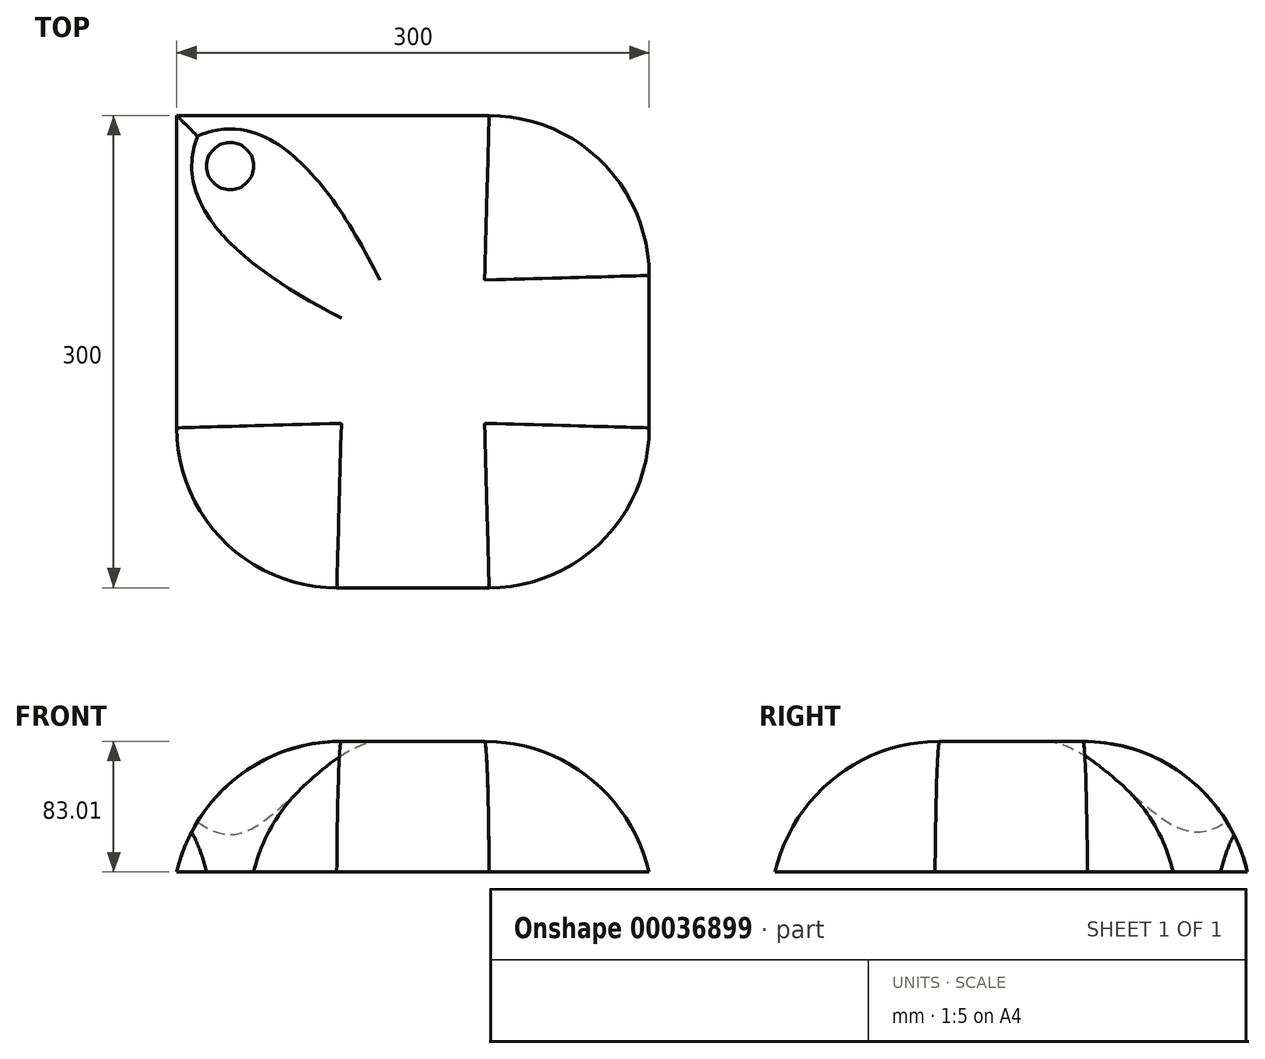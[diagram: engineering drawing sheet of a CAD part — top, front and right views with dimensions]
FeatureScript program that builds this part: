
annotation { "Feature Type Name" : "Feature", "Feature Type Description" : "" }
export const myFeature = defineFeature(function(context is Context, id is Id, definition is map)
    precondition{}
    {
        {
            var Q0;
            Q0=qCreatedBy(makeId("Top.planeOp"),FACE);
            var sketch = newSketch(context, id + "F0", { "sketchPlane" : qUnion([Q0])});
            skLineSegment(sketch, "E0.bottom", {"start": v(-153.37, 144.8) * mm, "end": v(146.63, 144.8) * mm});
            skLineSegment(sketch, "E0.top", {"start": v(-153.37, -155.2) * mm, "end": v(146.63, -155.2) * mm});
            skLineSegment(sketch, "E0.left", {"start": v(-153.37, 144.8) * mm, "end": v(-153.37, -155.2) * mm});
            skLineSegment(sketch, "E0.right", {"start": v(146.63, 144.8) * mm, "end": v(146.63, -155.2) * mm});
            skCircle(sketch, "E1", {"center": v(-119.5, 112.69) * mm, "radius": 15 * mm});
            skSolve(sketch);
        }
        {
            var Q0;
            Q0 = qSketchRegion(id + "F0", true);
            var Q1;
            Q1=makeQuery(id+"F0.imprint","IMPRINT",FACE,{"disambiguationData":[TD([[makeQuery(id+"F0.imprint","IMPRINT",EDGE,{"derivedFrom":sQuery(id+"F0.wireOp",EDGE,"E0.bottom")}),-1.0]])]});
            extrude(context, id + "F1", {"entities" : qUnion([Q0, Q1]), "depth" : 83.01 * mm});
        }
        {
            var Q0;
            Q0=makeQuery(id+"F1.opExtrude","SWEPT_EDGE",EDGE,{"disambiguationData":[OSD([sQuery(id+"F0.wireOp",EDGE,"E0.bottom"),sQuery(id+"F0.wireOp",EDGE,"E0.right")])]});
            var Q1;
            Q1=makeQuery(id+"F1.opExtrude","SWEPT_EDGE",EDGE,{"disambiguationData":[OSD([sQuery(id+"F0.wireOp",EDGE,"E0.top"),sQuery(id+"F0.wireOp",EDGE,"E0.left")])]});
            var Q2;
            Q2=makeQuery(id+"F1.opExtrude","SWEPT_EDGE",EDGE,{"disambiguationData":[OSD([sQuery(id+"F0.wireOp",EDGE,"E0.top"),sQuery(id+"F0.wireOp",EDGE,"E0.right")])]});
            fillet(context, id + "F2", {"entities" : qUnion([Q0, Q1, Q2]), "radius" : 101.6 * mm, "tangentPropagation" : true, "allowEdgeOverflow" : false});
        }
        {
            var Q0;
            Q0=makeQuery(id+"F1.opExtrude","CAP_FACE",FACE,{"disambiguationData":[OSD([sQuery(id+"F0.wireOp",EDGE,"E0.bottom"),sQuery(id+"F0.wireOp",EDGE,"E0.top"),sQuery(id+"F0.wireOp",EDGE,"E0.left"),sQuery(id+"F0.wireOp",EDGE,"E0.right"),sQuery(id+"F0.wireOp",EDGE,"E1")])],"isStart":false});
            fillet(context, id + "F3", {"entities" : qUnion([Q0]), "radius" : 107.3 * mm, "tangentPropagation" : true, "allowEdgeOverflow" : false});
        }
    });
